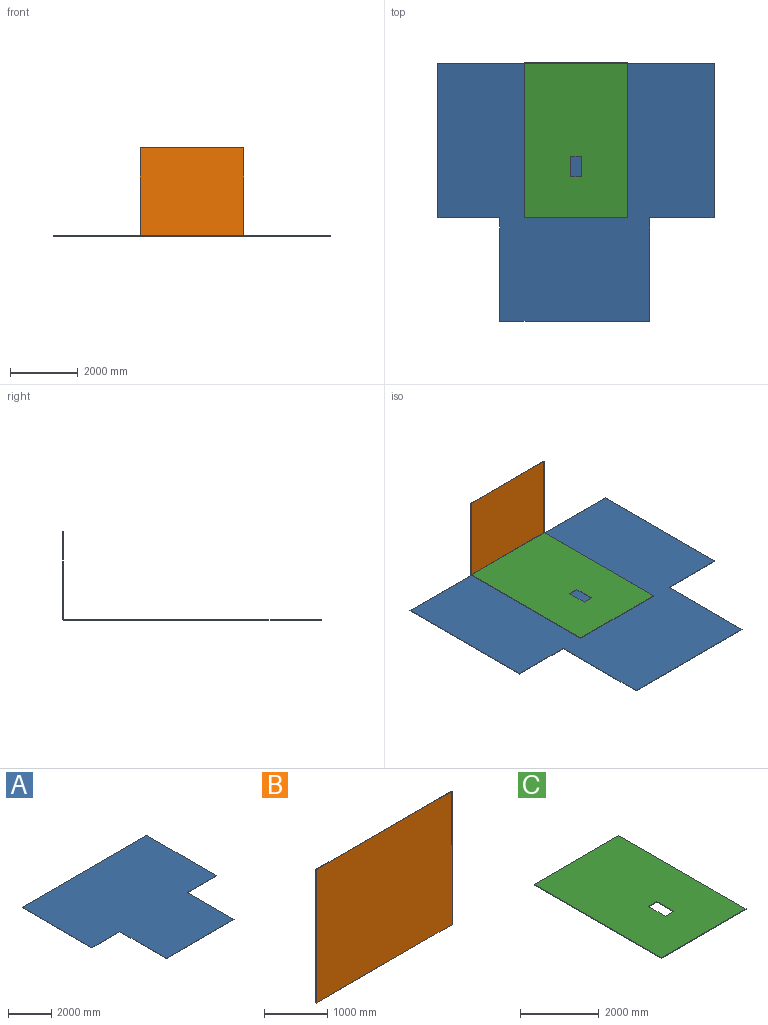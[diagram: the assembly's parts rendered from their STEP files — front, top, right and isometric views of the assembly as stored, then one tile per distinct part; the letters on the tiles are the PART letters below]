
ASSEMBLY  parts=3 mates=2
PART A: 10 faces, bbox 8153.4x7620x12.7 mm
  f0: plane 4572x12.7mm, normal (-1,0,0), area 58064.4mm2, adj f1,f7,f8,f9
  f1: plane 1828.8x12.7mm, normal (0,-1,0), area 23225.8mm2, adj f0,f2,f8,f9
  f2: plane 3048x12.7mm, normal (-1,0,0), area 38709.6mm2, adj f1,f3,f8,f9
  f3: plane 4419.6x12.7mm, normal (0,-1,0), area 56128.9mm2, adj f2,f4,f8,f9
  f4: plane 3048x12.7mm, normal (1,0,0), area 38709.6mm2, adj f3,f5,f8,f9
  f5: plane 1905x12.7mm, normal (0,-1,0), area 24193.5mm2, adj f4,f6,f8,f9
  f6: plane 4572x12.7mm, normal (1,0,0), area 58064.4mm2, adj f5,f7,f8,f9
  f7: plane 8153.4x12.7mm, normal (0,1,0), area 103548.2mm2, adj f0,f6,f8,f9
  f8: plane 8153.4x7620mm, normal (0,0,1), area 50748285.6mm2, adj f0,f1,f2,f3,f4,f5,f6,f7
  f9: plane 8153.4x7620mm, normal (0,0,-1), area 50748285.6mm2, adj f0,f1,f2,f3,f4,f5,f6,f7
PART B: 6 faces, bbox 3048x6.4x2590.8 mm
  f0: plane 3048x6.35mm, normal (0,0,1), area 19354.8mm2, adj f1,f3,f4,f5
  f1: plane 2590.8x6.35mm, normal (-1,0,0), area 16451.6mm2, adj f0,f2,f4,f5
  f2: plane 3048x6.35mm, normal (0,0,-1), area 19354.8mm2, adj f1,f3,f4,f5
  f3: plane 2590.8x6.35mm, normal (1,0,0), area 16451.6mm2, adj f0,f2,f4,f5
  f4: plane 3048x2590.8mm, normal (0,-1,0), area 7896758.4mm2, adj f0,f1,f2,f3
  f5: plane 3048x2590.8mm, normal (0,1,0), area 7896758.4mm2, adj f0,f1,f2,f3
PART C: 10 faces, bbox 3048x4572x19.1 mm
  f0: plane 4572x3048mm, normal (0,0,1), area 13749649.9mm2, adj f2,f3,f4,f5,f6,f7,f8,f9
  f1: plane 4572x3048mm, normal (0,0,-1), area 13749649.9mm2, adj f2,f3,f4,f5,f6,f7,f8,f9
  f2: plane 3048x19.05mm, normal (0,1,0), area 58064.4mm2, adj f0,f1,f3,f5
  f3: plane 4572x19.05mm, normal (-1,0,0), area 87096.6mm2, adj f0,f1,f2,f4
  f4: plane 3048x19.05mm, normal (0,-1,0), area 58064.4mm2, adj f0,f1,f3,f5
  f5: plane 4572x19.05mm, normal (1,0,0), area 87096.6mm2, adj f0,f1,f2,f4
  f6: plane 304.8x19.05mm, normal (0,-1,0), area 5806.4mm2, adj f0,f1,f7,f9
  f7: plane 609.6x19.05mm, normal (1,0,0), area 11612.9mm2, adj f0,f1,f6,f8
  f8: plane 304.8x19.05mm, normal (0,1,0), area 5806.4mm2, adj f0,f1,f7,f9
  f9: plane 609.6x19.05mm, normal (-1,0,0), area 11612.9mm2, adj f0,f1,f6,f8
PLACE A t=(-4009.99,2890.06,-305.31)mm
PLACE B t=(-1457.29,2896.41,2307.72)mm
PLACE C t=(-1457.29,2890.06,-292.61)mm
MATE fastened B.f4 <-> C.f2  axis (0,-1,0) through (66.71,2890.06,-283.08)mm
MATE fastened A.f8 <-> C.f1  axis (0,0,1) through (66.71,2890.06,-292.61)mm
